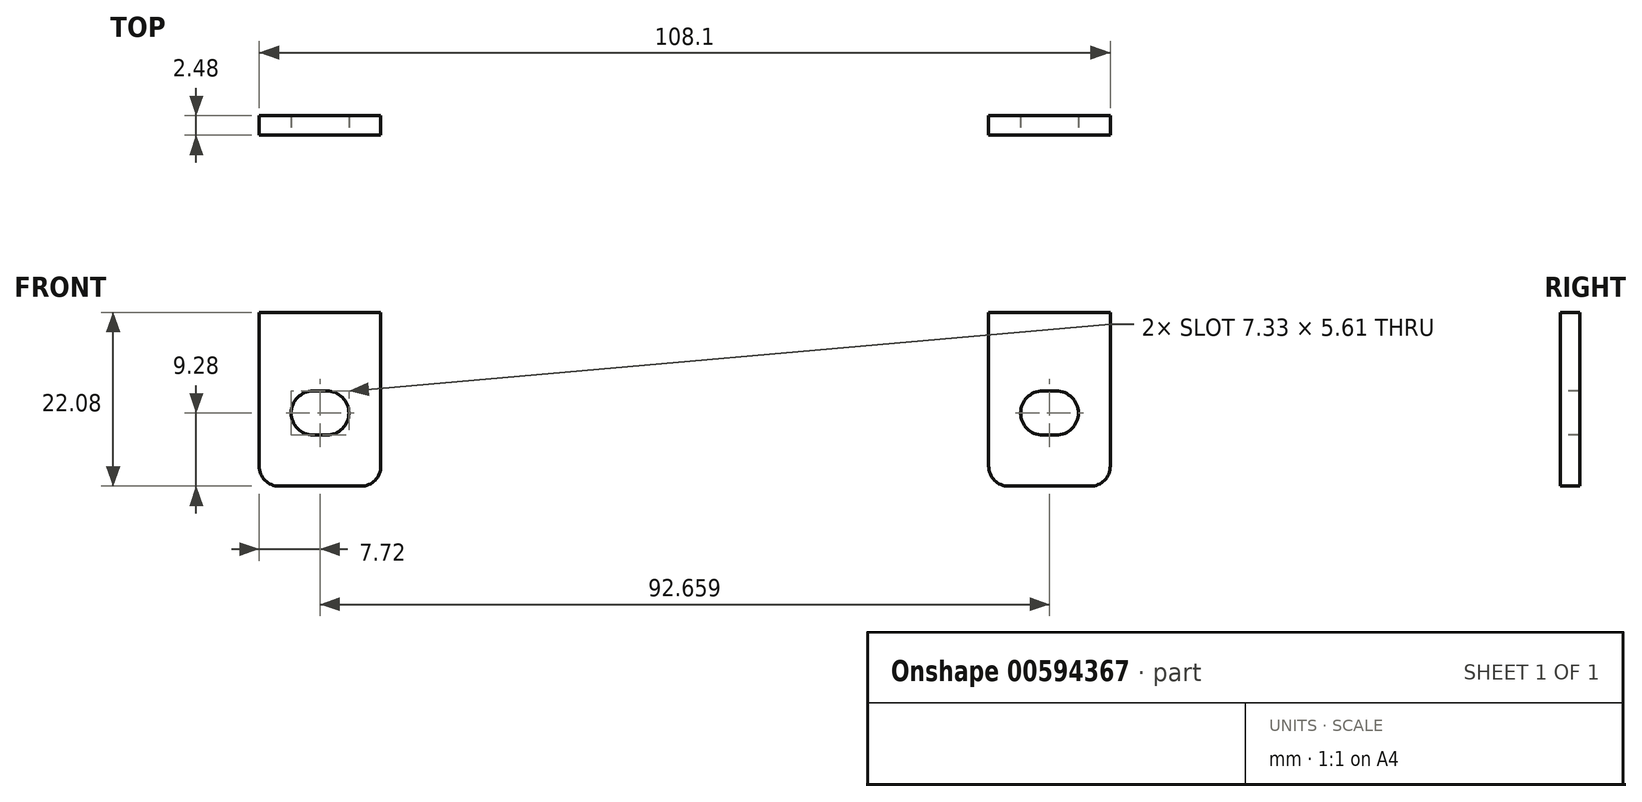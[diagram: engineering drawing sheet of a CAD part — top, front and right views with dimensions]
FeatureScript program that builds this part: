
annotation { "Feature Type Name" : "Feature", "Feature Type Description" : "" }
export const myFeature = defineFeature(function(context is Context, id is Id, definition is map)
    precondition{}
    {
        {
            var Q0;
            Q0=qCreatedBy(makeId("Top.planeOp"),FACE);
            var sketch = newSketch(context, id + "F0", { "sketchPlane" : qUnion([Q0])});
            skLineSegment(sketch, "E0", {"start": v(0, 0) * mm, "end": v(62.5, 0) * mm});
            skLineSegment(sketch, "E1", {"start": v(0, 0) * mm, "end": v(-62.5, 0) * mm});
            skPoint(sketch, "E2.visualSharp", {"position": v(-67.7, 0) * mm});
            skPoint(sketch, "E3.visualSharp", {"position": v(67.7, 0) * mm});
            skArc(sketch, "E4.MirrorCS", {"start": v(-67.01, -5.33) * mm, "mid": v(-66, -1.62) * mm, "end": v(-62.5, 0) * mm});
            skArc(sketch, "E5.MirrorCS", {"start": v(67.01, -5.33) * mm, "mid": v(0, -61.99) * mm, "end": v(-67.01, -5.33) * mm});
            skArc(sketch, "E6.MirrorCS", {"start": v(62.5, 0) * mm, "mid": v(66, -1.62) * mm, "end": v(67.01, -5.33) * mm});
            skPoint(sketch, "E2.filletArc.start.orphan", {"position": v(-67.01, 5.33) * mm});
            skPoint(sketch, "E3.filletArc.end.orphan", {"position": v(67.01, 5.33) * mm});
            skSolve(sketch);
        }
        {
            var Q0;
            Q0=qCreatedBy(makeId("Right.planeOp"),FACE);
            var sketch = newSketch(context, id + "F1", { "sketchPlane" : qUnion([Q0])});
            skCircle(sketch, "E7", {"center": v(0, 0) * mm, "radius": 2.29 * mm});
            skSolve(sketch);
        }
        {
            var Q0;
            Q0=makeQuery(id+"F1.imprint","IMPRINT",FACE,{"disambiguationData":[TD([[makeQuery(id+"F1.imprint","IMPRINT",EDGE,{"derivedFrom":sQuery(id+"F1.wireOp",EDGE,"E7")}),1.0]])]});
            var Q1;
            Q1=sQuery(id+"F0.wireOp",EDGE,"E0");
            var Q2;
            Q2=sQuery(id+"F0.wireOp",EDGE,"E6.MirrorCS");
            var Q3;
            Q3=sQuery(id+"F0.wireOp",EDGE,"E5.MirrorCS");
            var Q4;
            Q4=sQuery(id+"F0.wireOp",EDGE,"E4.MirrorCS");
            var Q5;
            Q5=sQuery(id+"F0.wireOp",EDGE,"E1");
            sweep(context, id + "F2", {"profiles" : qUnion([Q0]), "path" : qUnion([Q1, Q2, Q3, Q4, Q5])});
        }
        {
            var Q0;
            Q0=qCreatedBy(makeId("Top.planeOp"),FACE);
            var sketch = newSketch(context, id + "F3", { "sketchPlane" : qUnion([Q0])});
            skCircle(sketch, "E8", {"center": v(26.04, -4.06) * mm, "radius": 2.07 * mm});
            skLineSegment(sketch, "E9", {"start": v(0, 0) * mm, "end": v(0, -25.96) * mm, "construction": true});
            skCircle(sketch, "E10.MirrorC", {"center": v(-26.04, -4.06) * mm, "radius": 2.07 * mm});
            skSolve(sketch);
        }
        {
            var Q0;
            Q0=makeQuery(id+"F3.imprint","IMPRINT",FACE,{"disambiguationData":[TD([[makeQuery(id+"F3.imprint","IMPRINT",EDGE,{"derivedFrom":sQuery(id+"F3.wireOp",EDGE,"E10.MirrorC")}),-1.0]])]});
            var Q1;
            Q1=makeQuery(id+"F3.imprint","IMPRINT",FACE,{"disambiguationData":[TD([[makeQuery(id+"F3.imprint","IMPRINT",EDGE,{"derivedFrom":sQuery(id+"F3.wireOp",EDGE,"E8")}),1.0]])]});
            extrude(context, id + "F4", {"entities" : qUnion([Q0, Q1]), "operationType" : NewBodyOperationType.ADD, "depth" : 177.1 * mm, "offsetDistance" : 25.4 * mm, "hasSecondDirection" : true, "secondDirectionOppositeDirection" : true, "secondDirectionDepth" : 2.3 * mm});
        }
        {
            var Q0;
            Q0=qCreatedBy(makeId("Top.planeOp"),FACE);
            var Q1;
            Q1=makeQuery(id+"F2.opSweep","SWEPT_FACE",FACE,{"disambiguationData":[OSD([sQuery(id+"F0.wireOp",EDGE,"E0"),sQuery(id+"F1.wireOp",EDGE,"E7")])]});
            cPlane(context, id + "F5", {"entities" : qUnion([Q0, Q1]), "cplaneType" : CPlaneType.LINE_ANGLE, "offset" : 25.4 * mm, "angle" : 19.65 * degree, "width" : 152.4 * mm, "height" : 152.4 * mm});
        }
        {
            var Q0;
            Q0=qCreatedBy(id+"F5.planeOp",FACE);
            cPlane(context, id + "F6", {"entities" : qUnion([Q0]), "cplaneType" : CPlaneType.OFFSET, "offset" : 165.1 * mm, "oppositeDirection" : true, "width" : 152.4 * mm, "height" : 152.4 * mm});
        }
        {
            var Q0;
            Q0=qCreatedBy(id+"F6.planeOp",FACE);
            var sketch = newSketch(context, id + "F7", { "sketchPlane" : qUnion([Q0])});
            skLineSegment(sketch, "E11", {"start": v(0, -58.17) * mm, "end": v(-74.75, -58.17) * mm});
            skLineSegment(sketch, "E12", {"start": v(0, -58.17) * mm, "end": v(74.75, -58.17) * mm});
            skArc(sketch, "E13", {"start": v(79.29, -54.18) * mm, "mid": v(0, 35.8) * mm, "end": v(-79.29, -54.18) * mm});
            skLineSegment(sketch, "E14", {"start": v(0, -58.17) * mm, "end": v(0, 35.8) * mm, "construction": true});
            skPoint(sketch, "E15.visualSharp", {"position": v(-78.68, -58.17) * mm});
            skArc(sketch, "E15.filletArc", {"start": v(-79.29, -54.18) * mm, "mid": v(-77.77, -57.03) * mm, "end": v(-74.75, -58.17) * mm});
            skPoint(sketch, "E16.visualSharp", {"position": v(78.68, -58.17) * mm});
            skArc(sketch, "E16.filletArc", {"start": v(74.75, -58.17) * mm, "mid": v(77.77, -57.03) * mm, "end": v(79.29, -54.18) * mm});
            skSolve(sketch);
        }
        {
            var Q0;
            Q0=qCreatedBy(makeId("Right.planeOp"),FACE);
            var sketch = newSketch(context, id + "F8", { "sketchPlane" : qUnion([Q0])});
            skCircle(sketch, "E17", {"center": v(0, 175.32) * mm, "radius": 2.29 * mm});
            skSolve(sketch);
        }
        {
            var Q0;
            Q0=makeQuery(id+"F8.imprint","IMPRINT",FACE,{"disambiguationData":[TD([[makeQuery(id+"F8.imprint","IMPRINT",EDGE,{"derivedFrom":sQuery(id+"F8.wireOp",EDGE,"E17")}),1.0]])]});
            var Q1;
            Q1=sQuery(id+"F7.wireOp",EDGE,"E12");
            var Q2;
            Q2=sQuery(id+"F7.wireOp",EDGE,"E16.filletArc");
            var Q3;
            Q3=sQuery(id+"F7.wireOp",EDGE,"E13");
            var Q4;
            Q4=sQuery(id+"F7.wireOp",EDGE,"E15.filletArc");
            var Q5;
            Q5=sQuery(id+"F7.wireOp",EDGE,"E11");
            sweep(context, id + "F9", {"operationType" : NewBodyOperationType.ADD, "profiles" : qUnion([Q0]), "path" : qUnion([Q1, Q2, Q3, Q4, Q5])});
        }
        {
            var Q0;
            Q0=qCreatedBy(makeId("Right.planeOp"),FACE);
            cPlane(context, id + "F10", {"entities" : qUnion([Q0]), "cplaneType" : CPlaneType.OFFSET, "offset" : (2.74 + (.162 / 2)) * mm, "width" : 152.4 * mm, "height" : 152.4 * mm});
        }
        {
            var Q0;
            Q0=qCreatedBy(id+"F10.planeOp",FACE);
            var sketch = newSketch(context, id + "F11", { "sketchPlane" : qUnion([Q0])});
            skLineSegment(sketch, "E18", {"start": v(0, 0) * mm, "end": v(-63.18, 0) * mm});
            skSolve(sketch);
        }
        {
            var Q0;
            Q0=qCreatedBy(id+"F10.planeOp",FACE);
            var Q1;
            Q1=sQuery(id+"F11.wireOp",EDGE,"E18");
            cPlane(context, id + "F12", {"entities" : qUnion([Q0, Q1]), "cplaneType" : CPlaneType.LINE_ANGLE, "offset" : 25.4 * mm, "angle" : 5 * degree, "oppositeDirection" : true, "width" : 152.4 * mm, "height" : 152.4 * mm});
        }
        {
            var Q0;
            Q0=qCreatedBy(id+"F12.planeOp",FACE);
            var sketch = newSketch(context, id + "F13", { "sketchPlane" : qUnion([Q0])});
            skLineSegment(sketch, "E19", {"start": v(0, 3.96) * mm, "end": v(12.22, 3.96) * mm});
            skLineSegment(sketch, "E20", {"start": v(12.22, 3.96) * mm, "end": v(12.22, 178.58) * mm});
            skSolve(sketch);
        }
        {
            var Q0;
            Q0=qCreatedBy(id+"F12.planeOp",FACE);
            var Q1;
            Q1=sQuery(id+"F11.wireOp",EDGE,"E18");
            cPlane(context, id + "F14", {"entities" : qUnion([Q0, Q1]), "cplaneType" : CPlaneType.LINE_ANGLE, "offset" : 25.4 * mm, "angle" : 90 * degree, "width" : 152.4 * mm, "height" : 152.4 * mm});
        }
        {
            var Q0;
            Q0=qCreatedBy(id+"F14.planeOp",FACE);
            var sketch = newSketch(context, id + "F15", { "sketchPlane" : qUnion([Q0])});
            skCircle(sketch, "E21", {"center": v(69.6, -12.22) * mm, "radius": 2.06 * mm});
            skSolve(sketch);
        }
        {
            var Q0;
            Q0=makeQuery(id+"F15.imprint","IMPRINT",FACE,{"disambiguationData":[TD([[makeQuery(id+"F15.imprint","IMPRINT",EDGE,{"derivedFrom":sQuery(id+"F15.wireOp",EDGE,"E21")}),1.0]])]});
            var Q1;
            Q1=sQuery(id+"F13.wireOp",EDGE,"E20");
            sweep(context, id + "F16", {"operationType" : NewBodyOperationType.ADD, "profiles" : qUnion([Q0]), "path" : qUnion([Q1])});
        }
        {
            var Q0;
            Q0=qCreatedBy(makeId("Right.planeOp"),FACE);
            var Q1;
            Q1=makeQuery(id+"F4.opExtrude","CAP_EDGE",EDGE,{"disambiguationData":[OSD([sQuery(id+"F3.wireOp",EDGE,"E8")])],"isStart":false});
            cPlane(context, id + "F17", {"entities" : qUnion([Q0, Q1]), "cplaneType" : CPlaneType.LINE_ANGLE, "offset" : 64.22 * mm, "angle" : 25 * degree, "oppositeDirection" : true, "width" : 152.4 * mm, "height" : 152.4 * mm});
        }
        {
            var Q0;
            Q0=qCreatedBy(id+"F17.planeOp",FACE);
            cPlane(context, id + "F18", {"entities" : qUnion([Q0]), "cplaneType" : CPlaneType.OFFSET, "offset" : 44.2 * mm, "oppositeDirection" : true, "width" : 152.4 * mm, "height" : 152.4 * mm});
        }
        {
            var Q0;
            Q0=qCreatedBy(id+"F18.planeOp",FACE);
            var sketch = newSketch(context, id + "F19", { "sketchPlane" : qUnion([Q0])});
            skLineSegment(sketch, "E22", {"start": v(-13.64, 0) * mm, "end": v(27.23, 0) * mm});
            skSolve(sketch);
        }
        {
            var Q0;
            Q0 = qBodyType(qCreatedBy(id + "F19" ,EDGE), BodyType.WIRE);
            var Q1;
            Q1=qCreatedBy(makeId("Right.planeOp"),FACE);
            cPlane(context, id + "F20", {"entities" : qUnion([Q0, Q1]), "cplaneType" : CPlaneType.LINE_ANGLE, "offset" : 25.4 * mm, "angle" : 5.75 * degree, "oppositeDirection" : true, "width" : 152.4 * mm, "height" : 152.4 * mm});
        }
        {
            var Q0;
            Q0=qCreatedBy(id+"F20.planeOp",FACE);
            var sketch = newSketch(context, id + "F21", { "sketchPlane" : qUnion([Q0])});
            skLineSegment(sketch, "E23", {"start": v(0, 4.6) * mm, "end": v(0, 176.04) * mm});
            skSolve(sketch);
        }
        {
            var Q0;
            Q0=qCreatedBy(id+"F20.planeOp",FACE);
            var Q1;
            Q1=sQuery(id+"F19.wireOp",EDGE,"E22");
            cPlane(context, id + "F22", {"entities" : qUnion([Q0, Q1]), "cplaneType" : CPlaneType.LINE_ANGLE, "offset" : 25.4 * mm, "angle" : 90 * degree, "width" : 152.4 * mm, "height" : 152.4 * mm});
        }
        {
            var Q0;
            Q0=qCreatedBy(id+"F22.planeOp",FACE);
            var sketch = newSketch(context, id + "F23", { "sketchPlane" : qUnion([Q0])});
            skCircle(sketch, "E24", {"center": v(64.77, -24.35) * mm, "radius": 2.06 * mm});
            skSolve(sketch);
        }
        {
            var Q0;
            Q0=makeQuery(id+"F23.imprint","IMPRINT",FACE,{"disambiguationData":[TD([[makeQuery(id+"F23.imprint","IMPRINT",EDGE,{"derivedFrom":sQuery(id+"F23.wireOp",EDGE,"E24")}),1.0]])]});
            var Q1;
            Q1=sQuery(id+"F21.wireOp",EDGE,"E23");
            sweep(context, id + "F24", {"operationType" : NewBodyOperationType.ADD, "profiles" : qUnion([Q0]), "path" : qUnion([Q1])});
        }
        {
            var Q0;
            Q0=qCreatedBy(makeId("Right.planeOp"),FACE);
            var Q1;
            Q1=makeQuery(id+"F4.opExtrude","CAP_EDGE",EDGE,{"disambiguationData":[OSD([sQuery(id+"F3.wireOp",EDGE,"E8")])],"isStart":false});
            cPlane(context, id + "F25", {"entities" : qUnion([Q0, Q1]), "cplaneType" : CPlaneType.LINE_ANGLE, "offset" : 25.4 * mm, "angle" : 35 * degree, "oppositeDirection" : true, "width" : 152.4 * mm, "height" : 152.4 * mm});
        }
        {
            var Q0;
            Q0=qCreatedBy(id+"F25.planeOp",FACE);
            cPlane(context, id + "F26", {"entities" : qUnion([Q0]), "cplaneType" : CPlaneType.OFFSET, "offset" : 45.72 * mm, "oppositeDirection" : true, "width" : 152.4 * mm, "height" : 152.4 * mm});
        }
        {
            var Q0;
            Q0=qCreatedBy(id+"F26.planeOp",FACE);
            var sketch = newSketch(context, id + "F27", { "sketchPlane" : qUnion([Q0])});
            skLineSegment(sketch, "E25", {"start": v(95.43, 0) * mm, "end": v(0, 0) * mm});
            skSolve(sketch);
        }
        {
            var Q0;
            Q0=qCreatedBy(id+"F26.planeOp",FACE);
            var Q1;
            Q1=sQuery(id+"F27.wireOp",EDGE,"E25");
            cPlane(context, id + "F28", {"entities" : qUnion([Q0, Q1]), "cplaneType" : CPlaneType.LINE_ANGLE, "offset" : 25.4 * mm, "angle" : 6.35 * degree, "width" : 152.4 * mm, "height" : 152.4 * mm});
        }
        {
            var Q0;
            Q0=qCreatedBy(id+"F28.planeOp",FACE);
            var sketch = newSketch(context, id + "F29", { "sketchPlane" : qUnion([Q0])});
            skLineSegment(sketch, "E26", {"start": v(-2.93, 4.83) * mm, "end": v(-2.93, 172.47) * mm});
            skSolve(sketch);
        }
        {
            var Q0;
            Q0=qCreatedBy(id+"F28.planeOp",FACE);
            var Q1;
            Q1=sQuery(id+"F27.wireOp",EDGE,"E25");
            cPlane(context, id + "F30", {"entities" : qUnion([Q0, Q1]), "cplaneType" : CPlaneType.LINE_ANGLE, "offset" : 25.4 * mm, "angle" : 90 * degree, "width" : 152.4 * mm, "height" : 152.4 * mm});
        }
        {
            var Q0;
            Q0=qCreatedBy(id+"F30.planeOp",FACE);
            var sketch = newSketch(context, id + "F31", { "sketchPlane" : qUnion([Q0])});
            skCircle(sketch, "E27", {"center": v(58.93, -34.81) * mm, "radius": 2.06 * mm});
            skSolve(sketch);
        }
        {
            var Q0;
            Q0=makeQuery(id+"F31.imprint","IMPRINT",FACE,{"disambiguationData":[TD([[makeQuery(id+"F31.imprint","IMPRINT",EDGE,{"derivedFrom":sQuery(id+"F31.wireOp",EDGE,"E27")}),1.0]])]});
            var Q1;
            Q1=sQuery(id+"F29.wireOp",EDGE,"E26");
            sweep(context, id + "F32", {"operationType" : NewBodyOperationType.ADD, "profiles" : qUnion([Q0]), "path" : qUnion([Q1])});
        }
        {
            var Q0;
            Q0=qCreatedBy(makeId("Right.planeOp"),FACE);
            cPlane(context, id + "F33", {"entities" : qUnion([Q0]), "cplaneType" : CPlaneType.OFFSET, "offset" : 54.32 * mm, "width" : 152.4 * mm, "height" : 152.4 * mm});
        }
        {
            var Q0;
            Q0=qCreatedBy(id+"F33.planeOp",FACE);
            var sketch = newSketch(context, id + "F34", { "sketchPlane" : qUnion([Q0])});
            skLineSegment(sketch, "E28", {"start": v(0, 0) * mm, "end": v(-63.17, 0) * mm});
            skSolve(sketch);
        }
        {
            var Q0;
            Q0=qCreatedBy(id+"F33.planeOp",FACE);
            var Q1;
            Q1=sQuery(id+"F34.wireOp",EDGE,"E28");
            cPlane(context, id + "F35", {"entities" : qUnion([Q0, Q1]), "cplaneType" : CPlaneType.LINE_ANGLE, "offset" : 25.4 * mm, "angle" : 6.5 * degree, "oppositeDirection" : true, "width" : 152.4 * mm, "height" : 152.4 * mm});
        }
        {
            var Q0;
            Q0=qCreatedBy(id+"F35.planeOp",FACE);
            var sketch = newSketch(context, id + "F36", { "sketchPlane" : qUnion([Q0])});
            skLineSegment(sketch, "E29", {"start": v(-2.29, 1.2) * mm, "end": v(39.4, 1.2) * mm});
            skLineSegment(sketch, "E30", {"start": v(43.96, 5.46) * mm, "end": v(55.1, 164.64) * mm});
            skLineSegment(sketch, "E31", {"start": v(0, 5.53) * mm, "end": v(-2.29, 5.53) * mm, "construction": true});
            skLineSegment(sketch, "E32", {"start": v(-2.29, 5.53) * mm, "end": v(-2.29, 1.2) * mm, "construction": true});
            skPoint(sketch, "E33.visualSharp", {"position": v(43.66, 1.2) * mm});
            skArc(sketch, "E33.filletArc", {"start": v(39.4, 1.2) * mm, "mid": v(42.52, 2.44) * mm, "end": v(43.96, 5.46) * mm});
            skSolve(sketch);
        }
        {
            var Q0;
            Q0=qCreatedBy(makeId("Front.planeOp"),FACE);
            cPlane(context, id + "F37", {"entities" : qUnion([Q0]), "cplaneType" : CPlaneType.OFFSET, "offset" : 2.3 * mm, "oppositeDirection" : true, "width" : 152.4 * mm, "height" : 152.4 * mm});
        }
        {
            var Q0;
            Q0=qCreatedBy(id+"F37.planeOp",FACE);
            var sketch = newSketch(context, id + "F38", { "sketchPlane" : qUnion([Q0])});
            skCircle(sketch, "E34", {"center": v(54.32, -4.2) * mm, "radius": 2.06 * mm});
            skSolve(sketch);
        }
        {
            var Q0;
            Q0=makeQuery(id+"F38.imprint","IMPRINT",FACE,{"disambiguationData":[TD([[makeQuery(id+"F38.imprint","IMPRINT",EDGE,{"derivedFrom":sQuery(id+"F38.wireOp",EDGE,"E34")}),1.0]])]});
            var Q1;
            Q1=sQuery(id+"F36.wireOp",EDGE,"E29");
            var Q2;
            Q2=sQuery(id+"F36.wireOp",EDGE,"E33.filletArc");
            var Q3;
            Q3=sQuery(id+"F36.wireOp",EDGE,"E30");
            sweep(context, id + "F39", {"operationType" : NewBodyOperationType.ADD, "profiles" : qUnion([Q0]), "path" : qUnion([Q1, Q2, Q3])});
        }
        {
            var Q0;
            Q0=qCreatedBy(makeId("Right.planeOp"),FACE);
            cPlane(context, id + "F40", {"entities" : qUnion([Q0]), "cplaneType" : CPlaneType.OFFSET, "offset" : 43.57 * mm, "width" : 152.4 * mm, "height" : 152.4 * mm});
        }
        {
            var Q0;
            Q0=qCreatedBy(id+"F40.planeOp",FACE);
            var sketch = newSketch(context, id + "F41", { "sketchPlane" : qUnion([Q0])});
            skLineSegment(sketch, "E35", {"start": v(0, -4.05) * mm, "end": v(-45.6, -4.05) * mm});
            skSolve(sketch);
        }
        {
            var Q0;
            Q0=qCreatedBy(id+"F40.planeOp",FACE);
            var Q1;
            Q1=sQuery(id+"F41.wireOp",EDGE,"E35");
            cPlane(context, id + "F42", {"entities" : qUnion([Q0, Q1]), "cplaneType" : CPlaneType.LINE_ANGLE, "offset" : 25.4 * mm, "angle" : 6 * degree, "oppositeDirection" : true, "width" : 152.4 * mm, "height" : 152.4 * mm});
        }
        {
            var Q0;
            Q0=qCreatedBy(id+"F42.planeOp",FACE);
            var sketch = newSketch(context, id + "F43", { "sketchPlane" : qUnion([Q0])});
            skLineSegment(sketch, "E36", {"start": v(48.1, 2.4) * mm, "end": v(48.1, 24.35) * mm});
            skSolve(sketch);
        }
        {
            var Q0;
            Q0=qCreatedBy(id+"F42.planeOp",FACE);
            var Q1;
            Q1=sQuery(id+"F43.wireOp",EDGE,"E36");
            cPlane(context, id + "F44", {"entities" : qUnion([Q0, Q1]), "cplaneType" : CPlaneType.LINE_ANGLE, "offset" : 25.4 * mm, "angle" : 50 * degree, "oppositeDirection" : true, "width" : 152.4 * mm, "height" : 152.4 * mm});
        }
        {
            var Q0;
            Q0=qCreatedBy(id+"F44.planeOp",FACE);
            var sketch = newSketch(context, id + "F45", { "sketchPlane" : qUnion([Q0])});
            skLineSegment(sketch, "E37", {"start": v(-8.65, 3.54) * mm, "end": v(19.59, 3.54) * mm});
            skSolve(sketch);
        }
        {
            var Q0;
            Q0=qCreatedBy(id+"F44.planeOp",FACE);
            var Q1;
            Q1=sQuery(id+"F45.wireOp",EDGE,"E37");
            cPlane(context, id + "F46", {"entities" : qUnion([Q0, Q1]), "cplaneType" : CPlaneType.LINE_ANGLE, "offset" : 25.4 * mm, "angle" : 95.75 * degree, "width" : 152.4 * mm, "height" : 152.4 * mm});
        }
        {
            var Q0;
            Q0=qCreatedBy(id+"F46.planeOp",FACE);
            var sketch = newSketch(context, id + "F47", { "sketchPlane" : qUnion([Q0])});
            skCircle(sketch, "E38", {"center": v(43.57, -49.53) * mm, "radius": 2.06 * mm});
            skSolve(sketch);
        }
        {
            var Q0;
            Q0=makeQuery(id+"F47.imprint","IMPRINT",FACE,{"disambiguationData":[TD([[makeQuery(id+"F47.imprint","IMPRINT",EDGE,{"derivedFrom":sQuery(id+"F47.wireOp",EDGE,"E38")}),1.0]])]});
            extrude(context, id + "F48", {"entities" : qUnion([Q0]), "operationType" : NewBodyOperationType.ADD, "depth" : 154.3 * mm, "offsetDistance" : 25.4 * mm, "hasSecondDirection" : true, "secondDirectionOppositeDirection" : true, "secondDirectionDepth" : 1.27 * mm});
        }
        {
            var Q0;
            Q0=qCreatedBy(makeId("Right.planeOp"),FACE);
            cPlane(context, id + "F49", {"entities" : qUnion([Q0]), "cplaneType" : CPlaneType.OFFSET, "offset" : 32.05 * mm, "width" : 152.4 * mm, "height" : 152.4 * mm});
        }
        {
            var Q0;
            Q0=qCreatedBy(id+"F49.planeOp",FACE);
            var sketch = newSketch(context, id + "F50", { "sketchPlane" : qUnion([Q0])});
            skLineSegment(sketch, "E39", {"start": v(0, 0) * mm, "end": v(-74.18, 0) * mm});
            skSolve(sketch);
        }
        {
            var Q0;
            Q0=qCreatedBy(id+"F49.planeOp",FACE);
            var Q1;
            Q1=sQuery(id+"F50.wireOp",EDGE,"E39");
            cPlane(context, id + "F51", {"entities" : qUnion([Q0, Q1]), "cplaneType" : CPlaneType.LINE_ANGLE, "offset" : 25.4 * mm, "angle" : 3 * degree, "oppositeDirection" : true, "width" : 152.4 * mm, "height" : 152.4 * mm});
        }
        {
            var Q0;
            Q0=qCreatedBy(id+"F51.planeOp",FACE);
            var sketch = newSketch(context, id + "F52", { "sketchPlane" : qUnion([Q0])});
            skLineSegment(sketch, "E40", {"start": v(-2.31, -2.54) * mm, "end": v(55.51, -2.54) * mm});
            skLineSegment(sketch, "E41", {"start": v(60.02, 1.27) * mm, "end": v(84.74, 149.02) * mm});
            skPoint(sketch, "E42.visualSharp", {"position": v(59.38, -2.54) * mm});
            skArc(sketch, "E42.filletArc", {"start": v(55.51, -2.54) * mm, "mid": v(58.47, -1.46) * mm, "end": v(60.02, 1.27) * mm});
            skSolve(sketch);
        }
        {
            var Q0;
            Q0=qCreatedBy(id+"F37.planeOp",FACE);
            var sketch = newSketch(context, id + "F53", { "sketchPlane" : qUnion([Q0])});
            skCircle(sketch, "E43", {"center": v(31.88, -4.3) * mm, "radius": 2.06 * mm});
            skSolve(sketch);
        }
        {
            var Q0;
            Q0=makeQuery(id+"F53.imprint","IMPRINT",FACE,{"disambiguationData":[TD([[makeQuery(id+"F53.imprint","IMPRINT",EDGE,{"derivedFrom":sQuery(id+"F53.wireOp",EDGE,"E43")}),1.0]])]});
            var Q1;
            Q1=sQuery(id+"F52.wireOp",EDGE,"E40");
            var Q2;
            Q2=sQuery(id+"F52.wireOp",EDGE,"E42.filletArc");
            var Q3;
            Q3=sQuery(id+"F52.wireOp",EDGE,"E41");
            sweep(context, id + "F54", {"operationType" : NewBodyOperationType.ADD, "profiles" : qUnion([Q0]), "path" : qUnion([Q1, Q2, Q3])});
        }
        {
            var Q0;
            Q0=qCreatedBy(makeId("Right.planeOp"),FACE);
            cPlane(context, id + "F55", {"entities" : qUnion([Q0]), "cplaneType" : CPlaneType.OFFSET, "offset" : 21.46 * mm, "width" : 152.4 * mm, "height" : 152.4 * mm});
        }
        {
            var Q0;
            Q0=qCreatedBy(id+"F55.planeOp",FACE);
            var sketch = newSketch(context, id + "F56", { "sketchPlane" : qUnion([Q0])});
            skLineSegment(sketch, "E44", {"start": v(0, 0) * mm, "end": v(-65.17, 0) * mm});
            skSolve(sketch);
        }
        {
            var Q0;
            Q0=qCreatedBy(id+"F55.planeOp",FACE);
            var Q1;
            Q1=sQuery(id+"F56.wireOp",EDGE,"E44");
            cPlane(context, id + "F57", {"entities" : qUnion([Q0, Q1]), "cplaneType" : CPlaneType.LINE_ANGLE, "offset" : 25.4 * mm, "angle" : 2 * degree, "width" : 152.4 * mm, "height" : 152.4 * mm});
        }
        {
            var Q0;
            Q0=qCreatedBy(id+"F57.planeOp",FACE);
            var Q1;
            Q1=sQuery(id+"F56.wireOp",EDGE,"E44");
            cPlane(context, id + "F58", {"entities" : qUnion([Q0, Q1]), "cplaneType" : CPlaneType.LINE_ANGLE, "offset" : 25.4 * mm, "angle" : 90 * degree, "width" : 152.4 * mm, "height" : 152.4 * mm});
        }
        {
            var Q0;
            Q0=qCreatedBy(id+"F58.planeOp",FACE);
            var sketch = newSketch(context, id + "F59", { "sketchPlane" : qUnion([Q0])});
            skLineSegment(sketch, "E45", {"start": v(12.73, -65.7) * mm, "end": v(30, -59.82) * mm});
            skLineSegment(sketch, "E46", {"start": v(0, 0) * mm, "end": v(21.36, -62.76) * mm, "construction": true});
            skLineSegment(sketch, "E47", {"start": v(0, 0) * mm, "end": v(14.4, 0) * mm, "construction": true});
            skSolve(sketch);
        }
        {
            var Q0;
            Q0=sQuery(id+"F59.wireOp",EDGE,"E45");
            var Q1;
            Q1=qCreatedBy(id+"F58.planeOp",FACE);
            cPlane(context, id + "F60", {"entities" : qUnion([Q0, Q1]), "cplaneType" : CPlaneType.LINE_ANGLE, "offset" : 25.4 * mm, "angle" : 11.25 * degree, "width" : 152.4 * mm, "height" : 152.4 * mm});
        }
        {
            var Q0;
            Q0=qCreatedBy(id+"F60.planeOp",FACE);
            var sketch = newSketch(context, id + "F61", { "sketchPlane" : qUnion([Q0])});
            skCircle(sketch, "E48", {"center": v(21, 61.86) * mm, "radius": 2.06 * mm});
            skSolve(sketch);
        }
        {
            var Q0;
            Q0=makeQuery(id+"F61.imprint","IMPRINT",FACE,{"disambiguationData":[TD([[makeQuery(id+"F61.imprint","IMPRINT",EDGE,{"derivedFrom":sQuery(id+"F61.wireOp",EDGE,"E48")}),1.0]])]});
            extrude(context, id + "F62", {"entities" : qUnion([Q0]), "operationType" : NewBodyOperationType.ADD, "oppositeDirection" : true, "depth" : 147.83 * mm, "offsetDistance" : 25.4 * mm, "hasSecondDirection" : true, "secondDirectionOppositeDirection" : false, "secondDirectionDepth" : 2.3 * mm});
        }
        {
            var Q0;
            Q0=qCreatedBy(makeId("Right.planeOp"),FACE);
            cPlane(context, id + "F63", {"entities" : qUnion([Q0]), "cplaneType" : CPlaneType.OFFSET, "offset" : 10.96 * mm, "width" : 152.4 * mm, "height" : 152.4 * mm});
        }
        {
            var Q0;
            Q0=qCreatedBy(id+"F63.planeOp",FACE);
            var sketch = newSketch(context, id + "F64", { "sketchPlane" : qUnion([Q0])});
            skLineSegment(sketch, "E49", {"start": v(2.29, -4.2) * mm, "end": v(-61.26, -4.2) * mm});
            skLineSegment(sketch, "E50", {"start": v(-65.74, -0.5) * mm, "end": v(-93.86, 144.16) * mm});
            skLineSegment(sketch, "E51", {"start": v(0, 0) * mm, "end": v(2.29, 0) * mm, "construction": true});
            skLineSegment(sketch, "E52", {"start": v(2.29, 0) * mm, "end": v(2.29, -4.2) * mm, "construction": true});
            skPoint(sketch, "E53.visualSharp", {"position": v(-65.02, -4.2) * mm});
            skArc(sketch, "E53.filletArc", {"start": v(-65.74, -0.5) * mm, "mid": v(-64.16, -3.15) * mm, "end": v(-61.26, -4.2) * mm});
            skSolve(sketch);
        }
        {
            var Q0;
            Q0=qCreatedBy(id+"F37.planeOp",FACE);
            var sketch = newSketch(context, id + "F65", { "sketchPlane" : qUnion([Q0])});
            skCircle(sketch, "E54", {"center": v(10.96, -4.2) * mm, "radius": 2.06 * mm});
            skSolve(sketch);
        }
        {
            var Q0;
            Q0=makeQuery(id+"F65.imprint","IMPRINT",FACE,{"disambiguationData":[TD([[makeQuery(id+"F65.imprint","IMPRINT",EDGE,{"derivedFrom":sQuery(id+"F65.wireOp",EDGE,"E54")}),1.0]])]});
            var Q1;
            Q1=sQuery(id+"F64.wireOp",EDGE,"E49");
            var Q2;
            Q2=sQuery(id+"F64.wireOp",EDGE,"E53.filletArc");
            var Q3;
            Q3=sQuery(id+"F64.wireOp",EDGE,"E50");
            sweep(context, id + "F66", {"operationType" : NewBodyOperationType.ADD, "profiles" : qUnion([Q0]), "path" : qUnion([Q1, Q2, Q3])});
        }
        {
            var Q0;
            Q0=qCreatedBy(makeId("Right.planeOp"),FACE);
            var sketch = newSketch(context, id + "F67", { "sketchPlane" : qUnion([Q0])});
            skLineSegment(sketch, "E55", {"start": v(0, 0) * mm, "end": v(-65.53, 0) * mm, "construction": true});
            skLineSegment(sketch, "E56", {"start": v(-65.53, 0) * mm, "end": v(-93.52, 143.99) * mm});
            skSolve(sketch);
        }
        {
            var Q0;
            Q0=qCreatedBy(makeId("Top.planeOp"),FACE);
            var sketch = newSketch(context, id + "F68", { "sketchPlane" : qUnion([Q0])});
            skCircle(sketch, "E57", {"center": v(0, -65.79) * mm, "radius": 2.06 * mm});
            skSolve(sketch);
        }
        {
            var Q0;
            Q0=makeQuery(id+"F68.imprint","IMPRINT",FACE,{"disambiguationData":[TD([[makeQuery(id+"F68.imprint","IMPRINT",EDGE,{"derivedFrom":sQuery(id+"F68.wireOp",EDGE,"E57")}),1.0]])]});
            var Q1;
            Q1=sQuery(id+"F67.wireOp",EDGE,"E56");
            sweep(context, id + "F69", {"operationType" : NewBodyOperationType.ADD, "profiles" : qUnion([Q0]), "path" : qUnion([Q1])});
        }
        {
            var Q0;
            Q0=makeQuery(id+"F2.opSweep","SWEPT_BODY",BODY,{"disambiguationData":[OSD([sQuery(id+"F0.wireOp",EDGE,"E1"),sQuery(id+"F1.wireOp",EDGE,"E7")])]});
            var Q1;
            Q1=qCreatedBy(makeId("Right.planeOp"),FACE);
            mirror(context, id + "F70", {"operationType" : NewBodyOperationType.ADD, "entities" : qUnion([Q0]), "mirrorPlane" : qUnion([Q1])});
        }
        {
            var Q0;
            Q0=qCreatedBy(id+"F37.planeOp",FACE);
            var sketch = newSketch(context, id + "F71", { "sketchPlane" : qUnion([Q0])});
            skLineSegment(sketch, "E58", {"start": v(0, 0) * mm, "end": v(0, 174.75) * mm, "construction": true});
            skLineSegment(sketch, "E59", {"start": v(0, 174.75) * mm, "end": v(-38.6, 174.75) * mm, "construction": true});
            skLineSegment(sketch, "E60.bottom", {"start": v(-38.6, 174.75) * mm, "end": v(-54.05, 174.75) * mm});
            skLineSegment(sketch, "E60.top", {"start": v(-38.6, 152.67) * mm, "end": v(-54.05, 152.67) * mm});
            skLineSegment(sketch, "E60.left", {"start": v(-38.6, 174.75) * mm, "end": v(-38.6, 152.67) * mm});
            skLineSegment(sketch, "E60.right", {"start": v(-54.05, 174.75) * mm, "end": v(-54.05, 152.67) * mm});
            skLineSegment(sketch, "E61.bottom", {"start": v(-45.47, 164.76) * mm, "end": v(-47.19, 164.76) * mm});
            skLineSegment(sketch, "E61.top", {"start": v(-45.47, 159.14) * mm, "end": v(-47.19, 159.14) * mm});
            skLineSegment(sketch, "E61.left", {"start": v(-42.67, 161.95) * mm, "end": v(-42.67, 161.95) * mm});
            skLineSegment(sketch, "E61.right", {"start": v(-50, 161.95) * mm, "end": v(-50, 161.95) * mm});
            skPoint(sketch, "E62.visualSharp", {"position": v(-42.67, 164.76) * mm});
            skArc(sketch, "E62.filletArc", {"start": v(-42.67, 161.95) * mm, "mid": v(-43.49, 163.94) * mm, "end": v(-45.47, 164.76) * mm});
            skPoint(sketch, "E63.visualSharp", {"position": v(-42.67, 159.14) * mm});
            skArc(sketch, "E63.filletArc", {"start": v(-45.47, 159.14) * mm, "mid": v(-43.49, 159.97) * mm, "end": v(-42.67, 161.95) * mm});
            skPoint(sketch, "E64.visualSharp", {"position": v(-50, 164.76) * mm});
            skArc(sketch, "E64.filletArc", {"start": v(-47.19, 164.76) * mm, "mid": v(-49.17, 163.94) * mm, "end": v(-50, 161.95) * mm});
            skPoint(sketch, "E65.visualSharp", {"position": v(-50, 159.14) * mm});
            skArc(sketch, "E65.filletArc", {"start": v(-50, 161.95) * mm, "mid": v(-49.17, 159.97) * mm, "end": v(-47.19, 159.14) * mm});
            skLineSegment(sketch, "E66.MirrorCS", {"start": v(38.6, 174.75) * mm, "end": v(38.6, 152.67) * mm});
            skLineSegment(sketch, "E67.MirrorCS", {"start": v(38.6, 174.75) * mm, "end": v(54.05, 174.75) * mm});
            skLineSegment(sketch, "E68.MirrorCS", {"start": v(54.05, 174.75) * mm, "end": v(54.05, 152.67) * mm});
            skLineSegment(sketch, "E69.MirrorCS", {"start": v(38.6, 152.67) * mm, "end": v(54.05, 152.67) * mm});
            skArc(sketch, "E70.MirrorCS", {"start": v(50, 161.95) * mm, "mid": v(49.17, 159.97) * mm, "end": v(47.19, 159.14) * mm});
            skLineSegment(sketch, "E71.MirrorCS", {"start": v(45.47, 159.14) * mm, "end": v(47.19, 159.14) * mm});
            skArc(sketch, "E72.MirrorCS", {"start": v(45.47, 159.14) * mm, "mid": v(43.49, 159.97) * mm, "end": v(42.67, 161.95) * mm});
            skArc(sketch, "E73.MirrorCS", {"start": v(42.67, 161.95) * mm, "mid": v(43.49, 163.94) * mm, "end": v(45.47, 164.76) * mm});
            skLineSegment(sketch, "E74.MirrorCS", {"start": v(45.47, 164.76) * mm, "end": v(47.19, 164.76) * mm});
            skArc(sketch, "E75.MirrorCS", {"start": v(47.19, 164.76) * mm, "mid": v(49.17, 163.94) * mm, "end": v(50, 161.95) * mm});
            skSolve(sketch);
        }
        {
            var Q0;
            Q0=makeQuery(id+"F71.imprint","IMPRINT",FACE,{"disambiguationData":[TD([[makeQuery(id+"F71.imprint","IMPRINT",EDGE,{"derivedFrom":sQuery(id+"F71.wireOp",EDGE,"E66.MirrorCS")}),1.0]])]});
            var Q1;
            Q1=makeQuery(id+"F71.imprint","IMPRINT",FACE,{"disambiguationData":[TD([[makeQuery(id+"F71.imprint","IMPRINT",EDGE,{"derivedFrom":sQuery(id+"F71.wireOp",EDGE,"E60.bottom")}),1.0]])]});
            extrude(context, id + "F72", {"entities" : qUnion([Q0, Q1]), "oppositeDirection" : true, "depth" : 2.03 * mm, "offsetDistance" : 25.4 * mm, "hasSecondDirection" : true, "secondDirectionOppositeDirection" : false, "secondDirectionDepth" : 0.44 * mm});
        }
        {
            var Q0;
            Q0=makeQuery(id+"F72.opExtrude","SWEPT_EDGE",EDGE,{"disambiguationData":[OSD([sQuery(id+"F71.wireOp",EDGE,"E60.top"),sQuery(id+"F71.wireOp",EDGE,"E60.right")])]});
            var Q1;
            Q1=makeQuery(id+"F72.opExtrude","SWEPT_EDGE",EDGE,{"disambiguationData":[OSD([sQuery(id+"F71.wireOp",EDGE,"E60.top"),sQuery(id+"F71.wireOp",EDGE,"E60.left")])]});
            var Q2;
            Q2=makeQuery(id+"F72.opExtrude","SWEPT_EDGE",EDGE,{"disambiguationData":[OSD([sQuery(id+"F71.wireOp",EDGE,"E66.MirrorCS"),sQuery(id+"F71.wireOp",EDGE,"E69.MirrorCS")])]});
            var Q3;
            Q3=makeQuery(id+"F72.opExtrude","SWEPT_EDGE",EDGE,{"disambiguationData":[OSD([sQuery(id+"F71.wireOp",EDGE,"E68.MirrorCS"),sQuery(id+"F71.wireOp",EDGE,"E69.MirrorCS")])]});
            fillet(context, id + "F73", {"entities" : qUnion([Q0, Q1, Q2, Q3]), "radius" : 2.54 * mm, "tangentPropagation" : true, "allowEdgeOverflow" : false});
        }
    });
